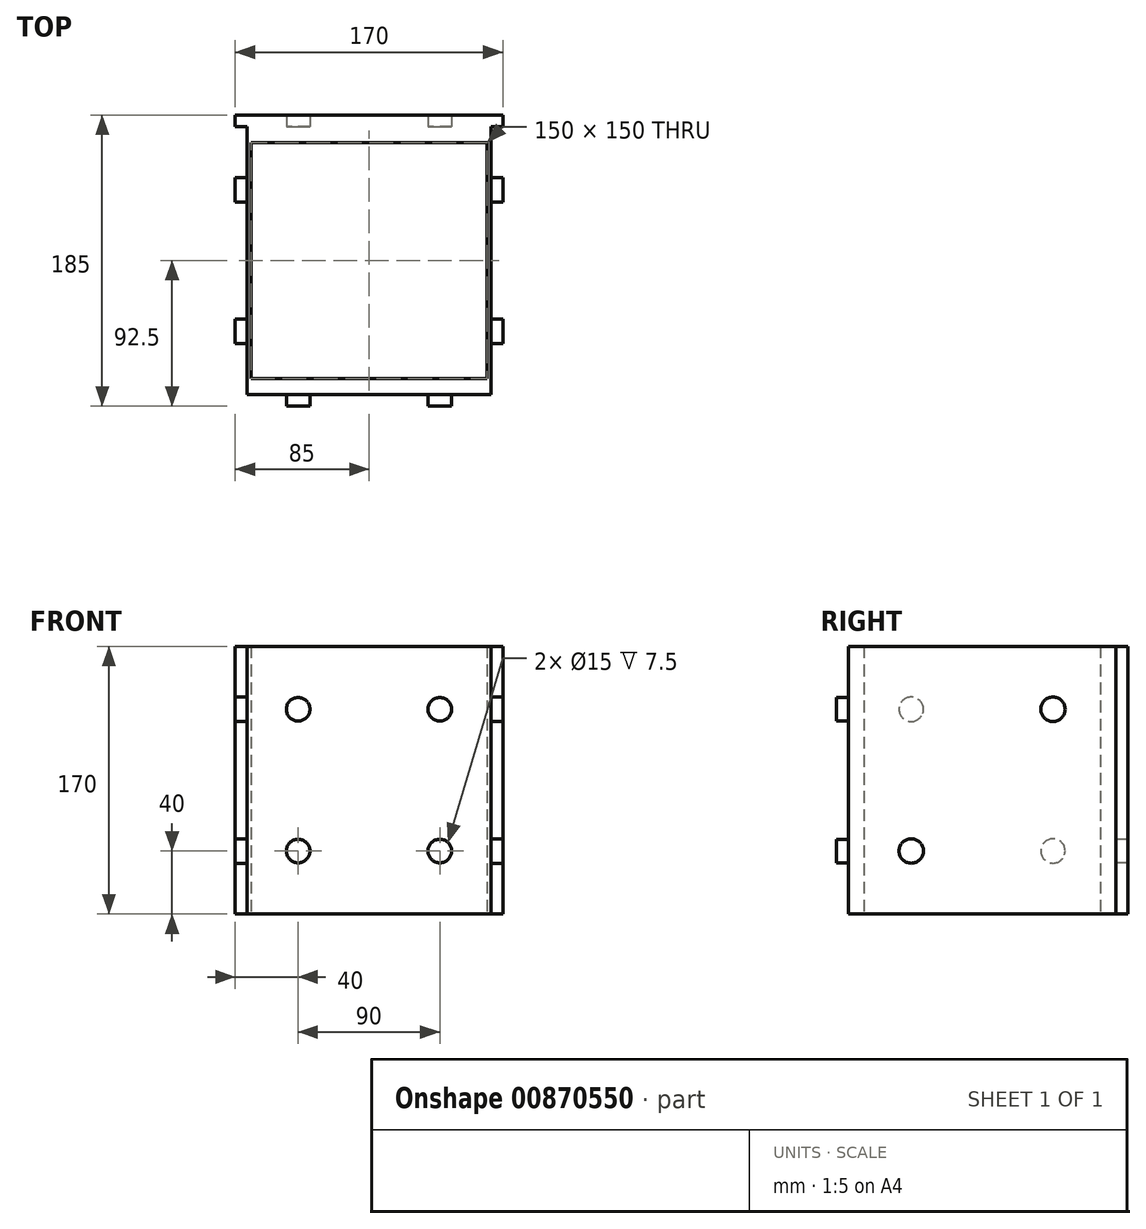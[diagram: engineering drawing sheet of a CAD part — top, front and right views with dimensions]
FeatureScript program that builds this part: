
annotation { "Feature Type Name" : "Feature", "Feature Type Description" : "" }
export const myFeature = defineFeature(function(context is Context, id is Id, definition is map)
    precondition{}
    {
        {
            var Q0;
            Q0=qCreatedBy(makeId("Top.planeOp"),FACE);
            var sketch = newSketch(context, id + "F0", { "sketchPlane" : qUnion([Q0])});
            skLineSegment(sketch, "E0.bottom", {"start": v(-85, 85) * mm, "end": v(85, 85) * mm});
            skLineSegment(sketch, "E0.top", {"start": v(-85, -85) * mm, "end": v(85, -85) * mm});
            skLineSegment(sketch, "E0.left", {"start": v(-85, 85) * mm, "end": v(-85, -85) * mm});
            skLineSegment(sketch, "E0.right", {"start": v(85, 85) * mm, "end": v(85, -85) * mm});
            skPoint(sketch, "E0.middle", {"position": v(0, 0) * mm});
            skSolve(sketch);
        }
        {
            var Q0;
            Q0=makeQuery(id+"F0.imprint","IMPRINT",FACE,{"disambiguationData":[TD([[makeQuery(id+"F0.imprint","IMPRINT",EDGE,{"derivedFrom":sQuery(id+"F0.wireOp",EDGE,"E0.bottom")}),-1.0]])]});
            extrude(context, id + "F1", {"entities" : qUnion([Q0]), "endBound" : BoundingType.SYMMETRIC, "depth" : 170 * mm, "offsetDistance" : 25 * mm});
        }
        {
            var Q0;
            Q0=qCreatedBy(makeId("Top.planeOp"),FACE);
            var sketch = newSketch(context, id + "F2", { "sketchPlane" : qUnion([Q0])});
            skLineSegment(sketch, "E1.bottom", {"start": v(-75, 75) * mm, "end": v(75, 75) * mm});
            skLineSegment(sketch, "E1.top", {"start": v(-75, -75) * mm, "end": v(75, -75) * mm});
            skLineSegment(sketch, "E1.left", {"start": v(-75, 75) * mm, "end": v(-75, -75) * mm});
            skLineSegment(sketch, "E1.right", {"start": v(75, 75) * mm, "end": v(75, -75) * mm});
            skPoint(sketch, "E1.middle", {"position": v(0, 0) * mm});
            skSolve(sketch);
        }
        {
            var Q0;
            Q0 = qSketchRegion(id + "F2", true);
            extrude(context, id + "F3", {"entities" : qUnion([Q0]), "operationType" : NewBodyOperationType.REMOVE, "endBound" : BoundingType.SYMMETRIC, "depth" : 170 * mm, "offsetDistance" : 25 * mm});
        }
        {
            var Q0;
            Q0=makeQuery(id+"F1.opExtrude","SWEPT_FACE",FACE,{"disambiguationData":[OSD([sQuery(id+"F0.wireOp",EDGE,"E0.right")])]});
            var sketch = newSketch(context, id + "F4", { "sketchPlane" : qUnion([Q0])});
            skLineSegment(sketch, "E2", {"start": v(0, 85) * mm, "end": v(0, -85) * mm, "construction": true});
            skLineSegment(sketch, "E3", {"start": v(-85, 0) * mm, "end": v(85, 0) * mm, "construction": true});
            skLineSegment(sketch, "E4", {"start": v(-85, 85) * mm, "end": v(85, -85) * mm, "construction": true});
            skLineSegment(sketch, "E5", {"start": v(85, 85) * mm, "end": v(-85, -85) * mm, "construction": true});
            skLineSegment(sketch, "E6", {"start": v(-85, 85) * mm, "end": v(-45, 85) * mm, "construction": true});
            skLineSegment(sketch, "E7.MirrorCS", {"start": v(-85, -85) * mm, "end": v(-45, -85) * mm, "construction": true});
            skLineSegment(sketch, "E8.MirrorCS", {"start": v(85, 85) * mm, "end": v(45, 85) * mm, "construction": true});
            skLineSegment(sketch, "E9.MirrorCS", {"start": v(85, -85) * mm, "end": v(45, -85) * mm, "construction": true});
            skLineSegment(sketch, "E10", {"start": v(-85, 85) * mm, "end": v(-85, 45) * mm, "construction": true});
            skLineSegment(sketch, "E11.MirrorCS", {"start": v(85, 85) * mm, "end": v(85, 45) * mm, "construction": true});
            skLineSegment(sketch, "E12.MirrorCS", {"start": v(-85, -85) * mm, "end": v(-85, -45) * mm, "construction": true});
            skLineSegment(sketch, "E13.MirrorCS", {"start": v(85, -85) * mm, "end": v(85, -45) * mm, "construction": true});
            skLineSegment(sketch, "E14", {"start": v(45, 85) * mm, "end": v(45, -85) * mm, "construction": true});
            skLineSegment(sketch, "E15", {"start": v(-85, 45) * mm, "end": v(85, 45) * mm, "construction": true});
            skLineSegment(sketch, "E16", {"start": v(-85, -45) * mm, "end": v(85, -45) * mm, "construction": true});
            skLineSegment(sketch, "E17", {"start": v(-45, 85) * mm, "end": v(-45, 45) * mm, "construction": true});
            skCircle(sketch, "E18", {"center": v(-45, 45) * mm, "radius": 7.75 * mm});
            skCircle(sketch, "E19.MirrorC", {"center": v(45, 45) * mm, "radius": 7.75 * mm});
            skCircle(sketch, "E20.MirrorC", {"center": v(-45, -45) * mm, "radius": 7.75 * mm});
            skCircle(sketch, "E21.MirrorC", {"center": v(45, -45) * mm, "radius": 7.75 * mm});
            skSolve(sketch);
        }
        {
            var Q0;
            Q0=makeQuery(id+"F1.opExtrude","SWEPT_FACE",FACE,{"disambiguationData":[OSD([sQuery(id+"F0.wireOp",EDGE,"E0.left")])]});
            var sketch = newSketch(context, id + "F5", { "sketchPlane" : qUnion([Q0])});
            skLineSegment(sketch, "E22", {"start": v(-85, 85) * mm, "end": v(-45, 85) * mm, "construction": true});
            skLineSegment(sketch, "E23", {"start": v(-85, 85) * mm, "end": v(-85, 45) * mm, "construction": true});
            skLineSegment(sketch, "E24", {"start": v(-45, 85) * mm, "end": v(-45, 45) * mm, "construction": true});
            skCircle(sketch, "E25", {"center": v(-45, 45) * mm, "radius": 7.75 * mm});
            skCircle(sketch, "E26.MirrorC", {"center": v(45, 45) * mm, "radius": 7.75 * mm});
            skCircle(sketch, "E27.MirrorC", {"center": v(-45, -45) * mm, "radius": 7.75 * mm});
            skCircle(sketch, "E28.MirrorC", {"center": v(45, -45) * mm, "radius": 7.75 * mm});
            skSolve(sketch);
        }
        {
            var Q0;
            Q0=makeQuery(id+"F1.opExtrude","SWEPT_FACE",FACE,{"disambiguationData":[OSD([sQuery(id+"F0.wireOp",EDGE,"E0.bottom")])]});
            var sketch = newSketch(context, id + "F6", { "sketchPlane" : qUnion([Q0])});
            skLineSegment(sketch, "E29", {"start": v(-85, 85) * mm, "end": v(-45, 85) * mm, "construction": true});
            skLineSegment(sketch, "E30.MirrorCS", {"start": v(85, 85) * mm, "end": v(45, 85) * mm, "construction": true});
            skLineSegment(sketch, "E31.MirrorCS", {"start": v(-85, -85) * mm, "end": v(-45, -85) * mm, "construction": true});
            skLineSegment(sketch, "E32.MirrorCS", {"start": v(85, -85) * mm, "end": v(45, -85) * mm, "construction": true});
            skLineSegment(sketch, "E33", {"start": v(-85, 85) * mm, "end": v(-85, 45) * mm, "construction": true});
            skLineSegment(sketch, "E34.MirrorCS", {"start": v(85, 85) * mm, "end": v(85, 45) * mm, "construction": true});
            skLineSegment(sketch, "E35.MirrorCS", {"start": v(-85, -85) * mm, "end": v(-85, -45) * mm, "construction": true});
            skLineSegment(sketch, "E36.MirrorCS", {"start": v(85, -85) * mm, "end": v(85, -45) * mm, "construction": true});
            skLineSegment(sketch, "E37", {"start": v(-85, 45) * mm, "end": v(-45, 45) * mm, "construction": true});
            skLineSegment(sketch, "E38.MirrorCS", {"start": v(-85, -45) * mm, "end": v(-45, -45) * mm, "construction": true});
            skLineSegment(sketch, "E39.MirrorCS", {"start": v(85, 45) * mm, "end": v(45, 45) * mm, "construction": true});
            skLineSegment(sketch, "E40.MirrorCS", {"start": v(85, -45) * mm, "end": v(45, -45) * mm, "construction": true});
            skCircle(sketch, "E41", {"center": v(-45, 45) * mm, "radius": 7.5 * mm});
            skCircle(sketch, "E42", {"center": v(45, 45) * mm, "radius": 7.5 * mm});
            skCircle(sketch, "E43.MirrorC", {"center": v(-45, -45) * mm, "radius": 7.5 * mm});
            skCircle(sketch, "E44.MirrorC", {"center": v(45, -45) * mm, "radius": 7.5 * mm});
            skSolve(sketch);
        }
        {
            var Q0;
            Q0=makeQuery(id+"F1.opExtrude","SWEPT_FACE",FACE,{"disambiguationData":[OSD([sQuery(id+"F0.wireOp",EDGE,"E0.top")])]});
            var sketch = newSketch(context, id + "F7", { "sketchPlane" : qUnion([Q0])});
            skLineSegment(sketch, "E45", {"start": v(-85, 85) * mm, "end": v(-85, 45) * mm, "construction": true});
            skLineSegment(sketch, "E46", {"start": v(-85, 85) * mm, "end": v(-45, 85) * mm, "construction": true});
            skLineSegment(sketch, "E47", {"start": v(-85, -85) * mm, "end": v(-85, -45) * mm, "construction": true});
            skLineSegment(sketch, "E48", {"start": v(-85, -85) * mm, "end": v(-45, -85) * mm, "construction": true});
            skLineSegment(sketch, "E49", {"start": v(85, 85) * mm, "end": v(45, 85) * mm, "construction": true});
            skLineSegment(sketch, "E50", {"start": v(85, 85) * mm, "end": v(85, 45) * mm, "construction": true});
            skLineSegment(sketch, "E51", {"start": v(85, -85) * mm, "end": v(85, -45) * mm, "construction": true});
            skLineSegment(sketch, "E52", {"start": v(85, -85) * mm, "end": v(45, -85) * mm, "construction": true});
            skLineSegment(sketch, "E53", {"start": v(-85, 45) * mm, "end": v(85, 45) * mm, "construction": true});
            skLineSegment(sketch, "E54", {"start": v(85, -45) * mm, "end": v(-85, -45) * mm, "construction": true});
            skLineSegment(sketch, "E55", {"start": v(-45, 85) * mm, "end": v(-45, 45) * mm, "construction": true});
            skLineSegment(sketch, "E56", {"start": v(45, 85) * mm, "end": v(45, 45) * mm, "construction": true});
            skLineSegment(sketch, "E57", {"start": v(-45, -85) * mm, "end": v(-45, -45) * mm, "construction": true});
            skLineSegment(sketch, "E58", {"start": v(45, -85) * mm, "end": v(45, -45) * mm, "construction": true});
            skCircle(sketch, "E59", {"center": v(-45, 45) * mm, "radius": 7.5 * mm});
            skCircle(sketch, "E60", {"center": v(45, 45) * mm, "radius": 7.5 * mm});
            skCircle(sketch, "E61", {"center": v(45, -45) * mm, "radius": 7.5 * mm});
            skCircle(sketch, "E62", {"center": v(-45, -45) * mm, "radius": 7.5 * mm});
            skSolve(sketch);
        }
        {
            var Q0;
            Q0=makeQuery(id+"F7.imprint","IMPRINT",FACE,{"disambiguationData":[TD([[makeQuery(id+"F7.imprint","IMPRINT",EDGE,{"derivedFrom":sQuery(id+"F7.wireOp",EDGE,"E59")}),1.0]])]});
            var Q1;
            Q1=makeQuery(id+"F7.imprint","IMPRINT",FACE,{"disambiguationData":[TD([[makeQuery(id+"F7.imprint","IMPRINT",EDGE,{"derivedFrom":sQuery(id+"F7.wireOp",EDGE,"E60")}),1.0]])]});
            var Q2;
            Q2=makeQuery(id+"F7.imprint","IMPRINT",FACE,{"disambiguationData":[TD([[makeQuery(id+"F7.imprint","IMPRINT",EDGE,{"derivedFrom":sQuery(id+"F7.wireOp",EDGE,"E61")}),1.0]])]});
            var Q3;
            Q3=makeQuery(id+"F7.imprint","IMPRINT",FACE,{"disambiguationData":[TD([[makeQuery(id+"F7.imprint","IMPRINT",EDGE,{"derivedFrom":sQuery(id+"F7.wireOp",EDGE,"E62")}),1.0]])]});
            extrude(context, id + "F8", {"entities" : qUnion([Q0, Q1, Q2, Q3]), "operationType" : NewBodyOperationType.ADD, "endBound" : BoundingType.SYMMETRIC, "depth" : 15 * mm, "offsetDistance" : 25 * mm});
        }
        {
            var Q0;
            Q0=makeQuery(id+"F6.imprint","IMPRINT",FACE,{"disambiguationData":[TD([[makeQuery(id+"F6.imprint","IMPRINT",EDGE,{"derivedFrom":sQuery(id+"F6.wireOp",EDGE,"E44.MirrorC")}),-1.0]])]});
            var Q1;
            Q1=makeQuery(id+"F6.imprint","IMPRINT",FACE,{"disambiguationData":[TD([[makeQuery(id+"F6.imprint","IMPRINT",EDGE,{"derivedFrom":sQuery(id+"F6.wireOp",EDGE,"E42")}),1.0]])]});
            var Q2;
            Q2=makeQuery(id+"F6.imprint","IMPRINT",FACE,{"disambiguationData":[TD([[makeQuery(id+"F6.imprint","IMPRINT",EDGE,{"derivedFrom":sQuery(id+"F6.wireOp",EDGE,"E41")}),1.0]])]});
            var Q3;
            Q3=makeQuery(id+"F6.imprint","IMPRINT",FACE,{"disambiguationData":[TD([[makeQuery(id+"F6.imprint","IMPRINT",EDGE,{"derivedFrom":sQuery(id+"F6.wireOp",EDGE,"E43.MirrorC")}),-1.0]])]});
            extrude(context, id + "F9", {"entities" : qUnion([Q0, Q1, Q2, Q3]), "operationType" : NewBodyOperationType.ADD, "endBound" : BoundingType.SYMMETRIC, "depth" : 15 * mm, "offsetDistance" : 25 * mm});
        }
        {
            var Q0;
            Q0=makeQuery(id+"F5.imprint","IMPRINT",FACE,{"disambiguationData":[TD([[makeQuery(id+"F5.imprint","IMPRINT",EDGE,{"derivedFrom":sQuery(id+"F5.wireOp",EDGE,"E25")}),1.0]])]});
            var Q1;
            Q1=makeQuery(id+"F5.imprint","IMPRINT",FACE,{"disambiguationData":[TD([[makeQuery(id+"F5.imprint","IMPRINT",EDGE,{"derivedFrom":sQuery(id+"F5.wireOp",EDGE,"E26.MirrorC")}),-1.0]])]});
            var Q2;
            Q2=makeQuery(id+"F5.imprint","IMPRINT",FACE,{"disambiguationData":[TD([[makeQuery(id+"F5.imprint","IMPRINT",EDGE,{"derivedFrom":sQuery(id+"F5.wireOp",EDGE,"E28.MirrorC")}),1.0]])]});
            var Q3;
            Q3=makeQuery(id+"F5.imprint","IMPRINT",FACE,{"disambiguationData":[TD([[makeQuery(id+"F5.imprint","IMPRINT",EDGE,{"derivedFrom":sQuery(id+"F5.wireOp",EDGE,"E27.MirrorC")}),-1.0]])]});
            extrude(context, id + "F10", {"entities" : qUnion([Q0, Q1, Q2, Q3]), "operationType" : NewBodyOperationType.REMOVE, "endBound" : BoundingType.SYMMETRIC, "depth" : 15 * mm, "offsetDistance" : 25 * mm});
        }
        {
            var Q0;
            Q0=makeQuery(id+"F4.imprint","IMPRINT",FACE,{"disambiguationData":[TD([[makeQuery(id+"F4.imprint","IMPRINT",EDGE,{"derivedFrom":sQuery(id+"F4.wireOp",EDGE,"E18")}),1.0]])]});
            var Q1;
            Q1=makeQuery(id+"F4.imprint","IMPRINT",FACE,{"disambiguationData":[TD([[makeQuery(id+"F4.imprint","IMPRINT",EDGE,{"derivedFrom":sQuery(id+"F4.wireOp",EDGE,"E19.MirrorC")}),-1.0]])]});
            var Q2;
            Q2=makeQuery(id+"F4.imprint","IMPRINT",FACE,{"disambiguationData":[TD([[makeQuery(id+"F4.imprint","IMPRINT",EDGE,{"derivedFrom":sQuery(id+"F4.wireOp",EDGE,"E21.MirrorC")}),1.0]])]});
            var Q3;
            Q3=makeQuery(id+"F4.imprint","IMPRINT",FACE,{"disambiguationData":[TD([[makeQuery(id+"F4.imprint","IMPRINT",EDGE,{"derivedFrom":sQuery(id+"F4.wireOp",EDGE,"E20.MirrorC")}),-1.0]])]});
            extrude(context, id + "F11", {"entities" : qUnion([Q0, Q1, Q2, Q3]), "operationType" : NewBodyOperationType.REMOVE, "endBound" : BoundingType.SYMMETRIC, "oppositeDirection" : true, "depth" : 15 * mm, "offsetDistance" : 25 * mm});
        }
    });
